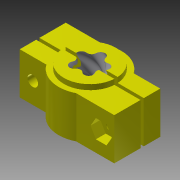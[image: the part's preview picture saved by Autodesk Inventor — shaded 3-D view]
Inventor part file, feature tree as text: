
AUTODESK INVENTOR PART (.ipt)
format: ipt  version: 2013 (Build 170138000, 138)  size: 2,034,176 bytes
history: native  units: mm
features: other x3, thread x1
ambient origin geometry x8: Origin, YZ Plane, XZ Plane, XY Plane, X Axis, Y Axis, Z Axis, Center Point
bodies: Solid1 (feature_tree)
feature tree (4):
  thread  "THREAD CLAMP SETUP.iam"  [1 undecoded]
  other  "_THREAD CLAMP.ipt:1"
  other  "_THREAD CLAMP.ipt:2"
  other  "7_16 TORQSPLINE.ipt:1"
note: 1 required parameter value undecoded (feature->parameter linkage not recoverable at this tier; creation-order binding heuristic only, values carry confidence <= 0.55)
